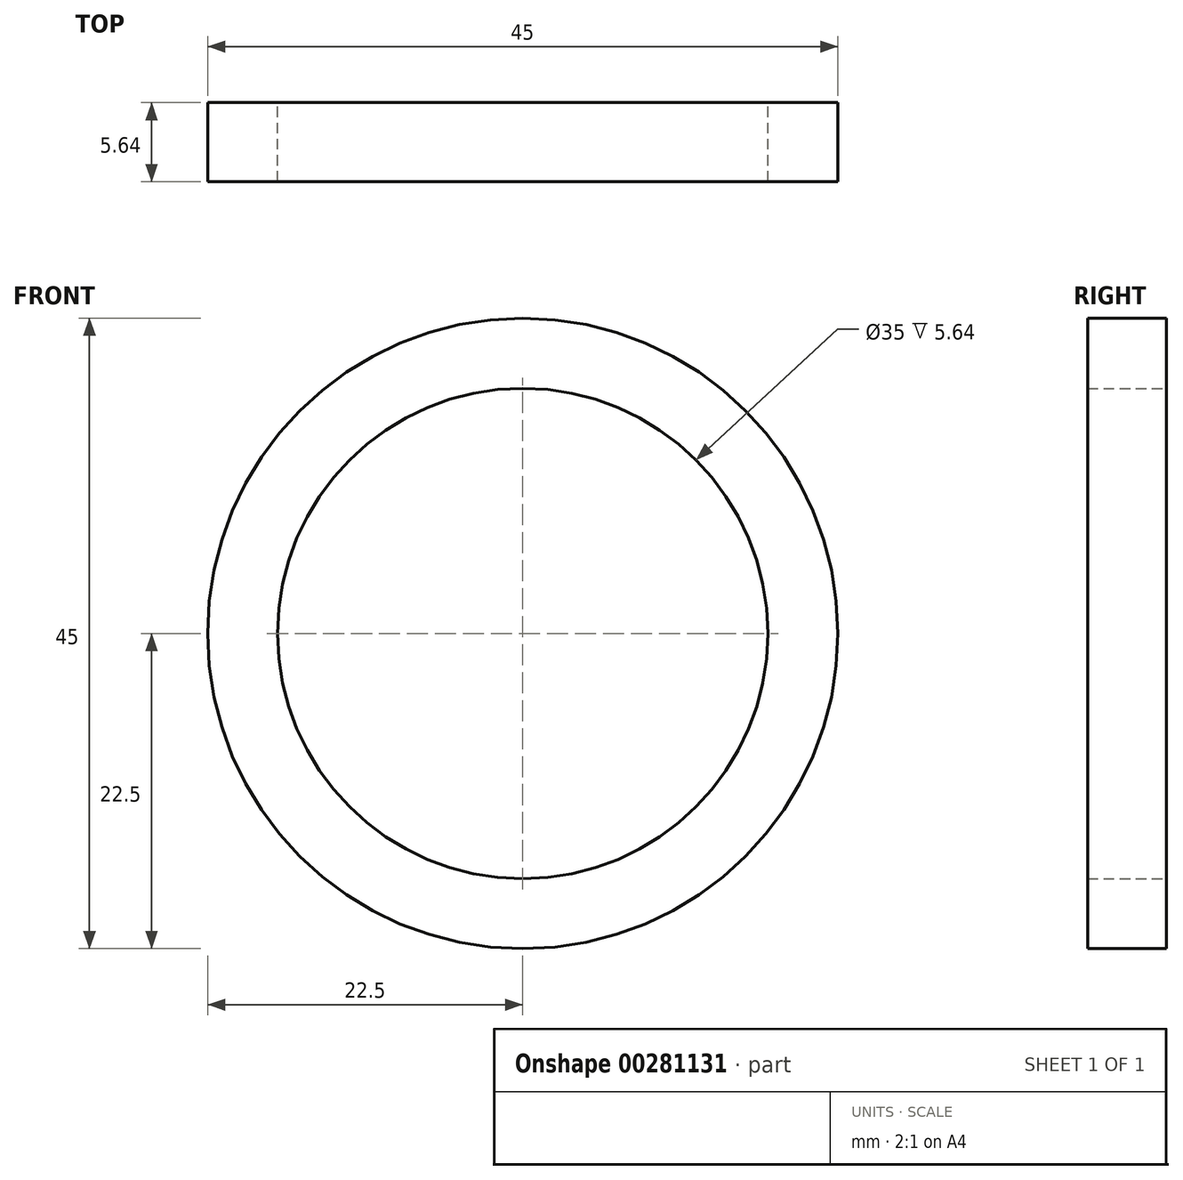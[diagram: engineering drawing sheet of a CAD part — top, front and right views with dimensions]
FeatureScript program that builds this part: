
annotation { "Feature Type Name" : "Feature", "Feature Type Description" : "" }
export const myFeature = defineFeature(function(context is Context, id is Id, definition is map)
    precondition{}
    {
        {
            var Q0;
            Q0=qCreatedBy(makeId("Front.planeOp"),FACE);
            var sketch = newSketch(context, id + "F0", { "sketchPlane" : qUnion([Q0])});
            skCircle(sketch, "E0", {"center": v(0, 0) * mm, "radius": 17.5 * mm});
            skCircle(sketch, "E1", {"center": v(0, 0) * mm, "radius": 22.5 * mm});
            skSolve(sketch);
        }
        {
            var Q0;
            Q0=makeQuery(id+"F0.imprint","IMPRINT",FACE,{"disambiguationData":[TD([[makeQuery(id+"F0.imprint","IMPRINT",EDGE,{"derivedFrom":sQuery(id+"F0.wireOp",EDGE,"E0")}),-1.0]])]});
            extrude(context, id + "F1", {"entities" : qUnion([Q0]), "depth" : 5.64 * mm});
        }
    });
